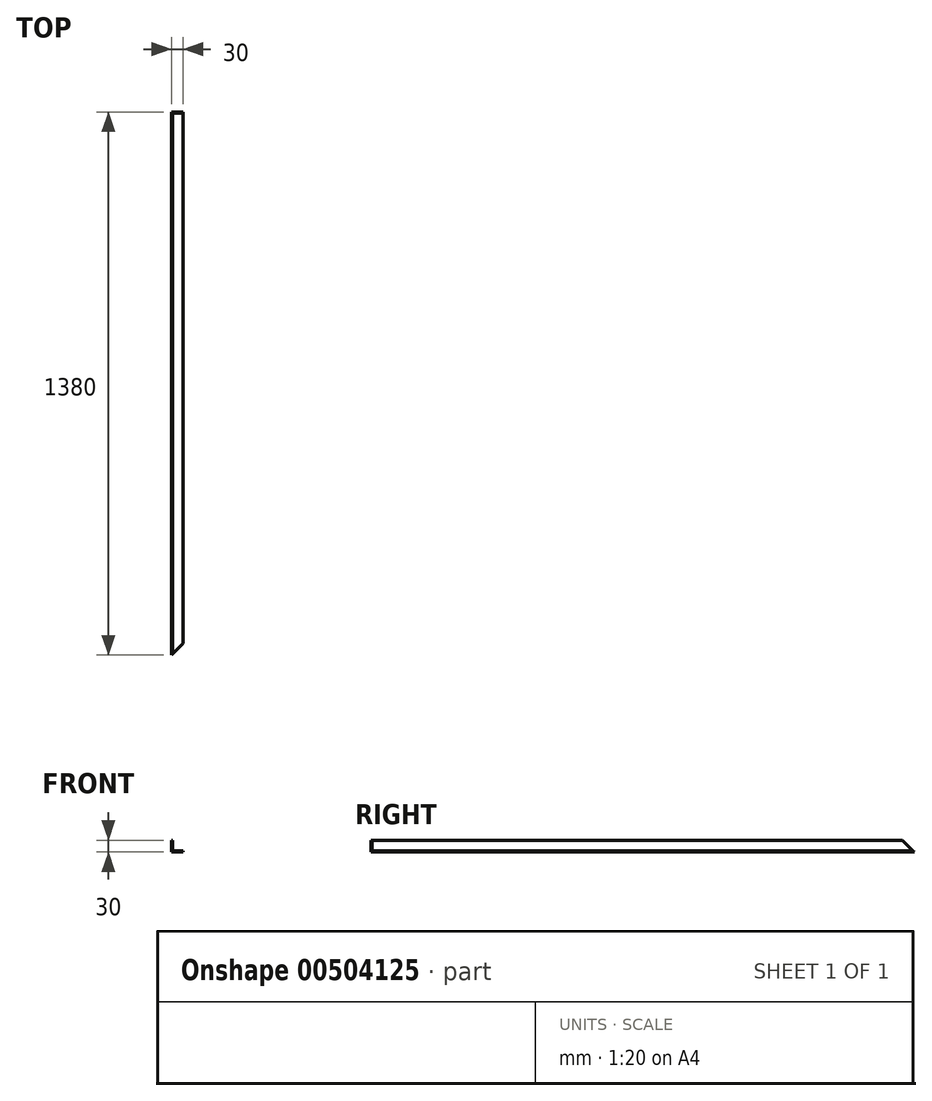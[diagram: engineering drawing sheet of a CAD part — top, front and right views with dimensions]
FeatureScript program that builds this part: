
annotation { "Feature Type Name" : "Feature", "Feature Type Description" : "" }
export const myFeature = defineFeature(function(context is Context, id is Id, definition is map)
    precondition{}
    {
        {
            var Q0;
            Q0=qCreatedBy(makeId("Front.planeOp"),FACE);
            var sketch = newSketch(context, id + "F0", { "sketchPlane" : qUnion([Q0])});
            skLineSegment(sketch, "E0", {"start": v(0, 0) * mm, "end": v(-30, 0) * mm});
            skLineSegment(sketch, "E1", {"start": v(-30, 0) * mm, "end": v(-30, 30) * mm});
            skLineSegment(sketch, "E2", {"start": v(-30, 30) * mm, "end": v(-27, 30) * mm});
            skLineSegment(sketch, "E3", {"start": v(-27, 30) * mm, "end": v(-27, 3) * mm});
            skLineSegment(sketch, "E4", {"start": v(-27, 3) * mm, "end": v(0, 3) * mm});
            skLineSegment(sketch, "E5", {"start": v(0, 3) * mm, "end": v(0, 0) * mm});
            skSolve(sketch);
        }
        {
            var Q0;
            Q0 = qSketchRegion(id + "F0", true);
            extrude(context, id + "F1", {"entities" : qUnion([Q0]), "oppositeDirection" : true, "depth" : 1380 * mm});
        }
        {
            var Q0;
            Q0=makeQuery(id+"F1.opExtrude","CAP_EDGE",EDGE,{"disambiguationData":[OSD([sQuery(id+"F0.wireOp",EDGE,"E5")])],"isStart":true});
            chamfer(context, id + "F2", {"entities" : qUnion([Q0]), "width" : 30 * mm, "tangentPropagation" : true});
        }
        {
            var Q0;
            Q0=makeQuery(id+"F1.opExtrude","CAP_EDGE",EDGE,{"disambiguationData":[OSD([sQuery(id+"F0.wireOp",EDGE,"E2")])],"isStart":false});
            chamfer(context, id + "F3", {"entities" : qUnion([Q0]), "width" : 30 * mm, "tangentPropagation" : true});
        }
    });
